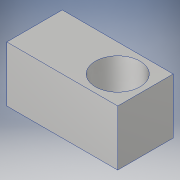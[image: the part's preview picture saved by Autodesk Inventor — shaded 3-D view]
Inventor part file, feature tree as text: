
AUTODESK INVENTOR PART (.ipt)
format: ipt  version: 2018 (Build 220112000, 112)  size: 97,792 bytes
history: native  units: in
note: dims shown in document units (in); Inventor stores cm internally (conversion verified against a paired STEP export)
features: sketch x2, extrude x1, hole x1
ambient origin geometry x8: Origin, YZ Plane, XZ Plane, XY Plane, X Axis, Y Axis, Z Axis, Center Point
bodies: Solid1 (feature_tree)
feature tree (4):
  extrude  "Extrusion1"  Depth=0.25in
  hole  "Hole1"  [1 undecoded]
  sketch  "Sketch1"  dims[d0=0.5in d1=0.25in]
  sketch  "Sketch2"  dims[d2=0.25in d3=0.0in d4=0.125in d5=0.201in d6=0.75in d7=0.385in d8=0.25in d9=0.5635in d10=1.0in d11=0.8108in]
note: 1 required parameter value undecoded (feature->parameter linkage not recoverable at this tier; creation-order binding heuristic only, values carry confidence <= 0.55)
